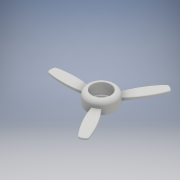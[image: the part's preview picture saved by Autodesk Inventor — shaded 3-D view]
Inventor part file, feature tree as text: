
AUTODESK INVENTOR PART (.ipt)
format: ipt  version: 2017 (Build 210142000, 142)  size: 312,320 bytes
history: native  units: mm
features: sketch x2, revolve x1, plane x1, extrude x1, draft x1, fillet x1, pattern_circular x1
ambient origin geometry x8: Origin, YZ Plane, XZ Plane, XY Plane, X Axis, Y Axis, Z Axis, Center Point
bodies: Solid1 (feature_tree)
feature tree (8):
  revolve  "Revolution1"  [1 undecoded]
  plane  "Work Plane1"
  extrude  "Extrusion1"  Depth=14.5mm
  draft  "FaceDraft1"
  fillet  "Fillet1"  Radius=3.0mm
  pattern_circular  "Circular Pattern1"  [2 undecoded]
  sketch  "Sketch1"  dims[d0=16.0mm d1=19.0mm]
  sketch  "Sketch2"  dims[d2=16.0mm d3=14.5mm d4=3.0mm d5=3.0mm d6=3.0mm d7=1.5mm d8=12.5mm d9=6.0mm d10=0.5mm d11=90.0deg d12=5.0mm d13=50.0mm d14=15.0mm d15=2.0mm d16=7.5mm d17=2.5mm d18=2.5mm d19=4.0mm d20=5.0mm d21=0.0mm d22=-0.174533mm d23=1.0mm d24=30.0mm d25=360.0deg]
note: 3 required parameter values undecoded (feature->parameter linkage not recoverable at this tier; creation-order binding heuristic only, values carry confidence <= 0.55)